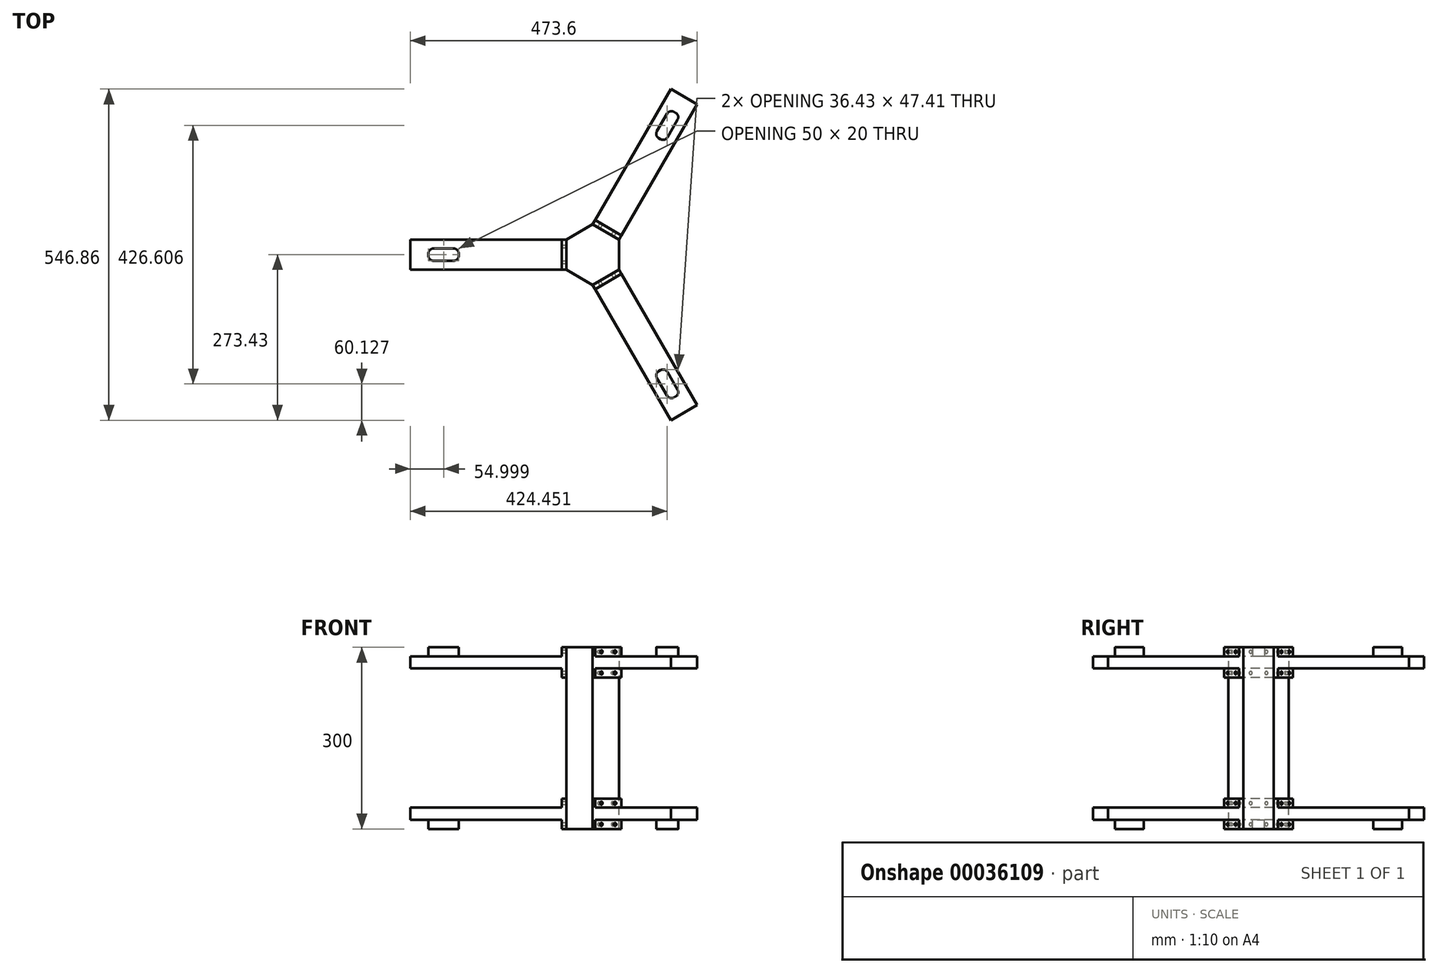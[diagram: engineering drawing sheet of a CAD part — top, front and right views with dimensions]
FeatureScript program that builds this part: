
annotation { "Feature Type Name" : "Feature", "Feature Type Description" : "" }
export const myFeature = defineFeature(function(context is Context, id is Id, definition is map)
    precondition{}
    {
        {
            var Q0;
            Q0=qCreatedBy(makeId("Top.planeOp"),FACE);
            var sketch = newSketch(context, id + "F0", { "sketchPlane" : qUnion([Q0])});
            skCircle(sketch, "E0.cCircle", {"center": v(0, 0) * mm, "radius": 50 * mm, "construction": true});
            skLineSegment(sketch, "E0.0", {"start": v(-43.3, 25) * mm, "end": v(0, 50) * mm});
            skLineSegment(sketch, "E0.1", {"start": v(0, 50) * mm, "end": v(43.3, 25) * mm});
            skLineSegment(sketch, "E0.2", {"start": v(43.3, 25) * mm, "end": v(43.3, -25) * mm});
            skLineSegment(sketch, "E0.3", {"start": v(43.3, -25) * mm, "end": v(0, -50) * mm});
            skLineSegment(sketch, "E0.4", {"start": v(0, -50) * mm, "end": v(-43.3, -25) * mm});
            skLineSegment(sketch, "E0.5", {"start": v(-43.3, -25) * mm, "end": v(-43.3, 25) * mm});
            skLineSegment(sketch, "E1", {"start": v(0, 50) * mm, "end": v(0, 0) * mm, "construction": true});
            skSolve(sketch);
        }
        {
            var Q0;
            Q0 = qSketchRegion(id + "F0", true);
            extrude(context, id + "F1", {"entities" : qUnion([Q0]), "endBound" : BoundingType.SYMMETRIC, "depth" : 300 * mm});
        }
        {
            var Q0;
            Q0=makeQuery(id+"F1.opExtrude","SWEPT_FACE",FACE,{"disambiguationData":[OSD([sQuery(id+"F0.wireOp",EDGE,"E0.3")])]});
            var sketch = newSketch(context, id + "F2", { "sketchPlane" : qUnion([Q0])});
            skLineSegment(sketch, "E2.bottom", {"start": v(-25, 150) * mm, "end": v(25, 150) * mm});
            skLineSegment(sketch, "E2.top", {"start": v(-25, 100) * mm, "end": v(25, 100) * mm});
            skLineSegment(sketch, "E2.left", {"start": v(-25, 150) * mm, "end": v(-25, 100) * mm});
            skLineSegment(sketch, "E2.right", {"start": v(25, 150) * mm, "end": v(25, 100) * mm});
            skSolve(sketch);
        }
        {
            var Q0;
            Q0=makeQuery(id+"F2.imprint","IMPRINT",FACE,{"disambiguationData":[TD([[makeQuery(id+"F2.imprint","IMPRINT",EDGE,{"derivedFrom":sQuery(id+"F2.wireOp",EDGE,"E2.bottom")}),1.0]])]});
            extrude(context, id + "F3", {"entities" : qUnion([Q0]), "depth" : 8 * mm});
        }
        {
            var Q0;
            Q0=makeQuery(id+"F3.opExtrude","CAP_FACE",FACE,{"disambiguationData":[OSD([sQuery(id+"F2.wireOp",EDGE,"E2.bottom"),sQuery(id+"F2.wireOp",EDGE,"E2.top"),sQuery(id+"F2.wireOp",EDGE,"E2.left"),sQuery(id+"F2.wireOp",EDGE,"E2.right")])],"isStart":false});
            var sketch = newSketch(context, id + "F4", { "sketchPlane" : qUnion([Q0])});
            skLineSegment(sketch, "E3.bottom", {"start": v(-25, 135) * mm, "end": v(25, 135) * mm});
            skLineSegment(sketch, "E3.top", {"start": v(-25, 115) * mm, "end": v(25, 115) * mm});
            skLineSegment(sketch, "E3.left", {"start": v(-25, 135) * mm, "end": v(-25, 115) * mm});
            skLineSegment(sketch, "E3.right", {"start": v(25, 135) * mm, "end": v(25, 115) * mm});
            skPoint(sketch, "E4", {"position": v(-25, 125) * mm});
            skSolve(sketch);
        }
        {
            var Q0;
            Q0 = qSketchRegion(id + "F4", true);
            extrude(context, id + "F5", {"entities" : qUnion([Q0]), "operationType" : NewBodyOperationType.ADD, "depth" : 250 * mm});
        }
        {
            var Q0;
            Q0=makeQuery(id+"F5.opExtrude","SWEPT_FACE",FACE,{"disambiguationData":[OSD([sQuery(id+"F4.wireOp",EDGE,"E3.bottom")])]});
            var Q1;
            Q1=makeQuery(id+"F5.opExtrude","SWEPT_FACE",FACE,{"disambiguationData":[OSD([sQuery(id+"F4.wireOp",EDGE,"E3.top")])]});
            cPlane(context, id + "F6", {"entities" : qUnion([Q0, Q1]), "cplaneType" : CPlaneType.MID_PLANE, "offset" : 150 * mm, "width" : 150 * mm, "height" : 150 * mm});
        }
        {
            var Q0;
            {var subQ0=sQuery(id+"F2.wireOp",EDGE,"E2.bottom");var subQ1=sQuery(id+"F2.wireOp",EDGE,"E2.left");var subQ2=sQuery(id+"F2.wireOp",EDGE,"E2.right");Q0=makeQuery(id+"F5.boolean.opBoolean","SPLIT",FACE,{"disambiguationData":[TD([makeQuery(id+"F3.opExtrude","SWEPT_FACE",FACE,{"disambiguationData":[OSD([subQ0])]})])],"derivedFrom":makeQuery(id+"F3.opExtrude","CAP_FACE",FACE,{"disambiguationData":[OSD([subQ0,sQuery(id+"F2.wireOp",EDGE,"E2.top"),subQ1,subQ2])],"isStart":false})});}
            var sketch = newSketch(context, id + "F7", { "sketchPlane" : qUnion([Q0])});
            skPoint(sketch, "E5", {"position": v(-13, 142.5) * mm});
            skPoint(sketch, "E6", {"position": v(13, 142.5) * mm});
            skLineSegment(sketch, "E7", {"start": v(-25, 142.5) * mm, "end": v(-13, 142.5) * mm});
            skLineSegment(sketch, "E8", {"start": v(13, 142.5) * mm, "end": v(-13, 142.5) * mm});
            skLineSegment(sketch, "E9", {"start": v(13, 142.5) * mm, "end": v(25, 142.5) * mm});
            skPoint(sketch, "E10.MirrorP", {"position": v(-13, 107.5) * mm});
            skPoint(sketch, "E11.MirrorP", {"position": v(13, 107.5) * mm});
            skSolve(sketch);
        }
        {
            var Q0;
            Q0=sQuery(id+"F7.wireOp",VERTEX,"E5");
            var Q1;
            Q1=sQuery(id+"F7.wireOp",VERTEX,"E6");
            var Q2;
            Q2=sQuery(id+"F7.wireOp",VERTEX,"E10.MirrorP");
            var Q3;
            Q3=sQuery(id+"F7.wireOp",VERTEX,"E11.MirrorP");
            var Q4;
            Q4=makeQuery(id+"F3.opExtrude","SWEPT_BODY",BODY,{"disambiguationData":[OSD([sQuery(id+"F2.wireOp",EDGE,"E2.bottom"),sQuery(id+"F2.wireOp",EDGE,"E2.top"),sQuery(id+"F2.wireOp",EDGE,"E2.left"),sQuery(id+"F2.wireOp",EDGE,"E2.right")])]});
            hole(context, id + "F8", {"style" : HoleStyle.SIMPLE, "holeDiameter" : 5 * mm, "endStyle" : HoleEndStyle.THROUGH, "locations" : qUnion([Q0, Q1, Q2, Q3]), "scope" : qUnion([Q4])});
        }
        {
            var Q0;
            Q0=makeQuery(id+"F5.opExtrude","SWEPT_FACE",FACE,{"disambiguationData":[OSD([sQuery(id+"F4.wireOp",EDGE,"E3.bottom")])]});
            var sketch = newSketch(context, id + "F9", { "sketchPlane" : qUnion([Q0])});
            skLineSegment(sketch, "E12", {"start": v(133.92, -235.95) * mm, "end": v(137.38, -233.95) * mm});
            skLineSegment(sketch, "E13", {"start": v(140.31, -223.03) * mm, "end": v(123.31, -193.58) * mm});
            skLineSegment(sketch, "E14", {"start": v(112.38, -190.65) * mm, "end": v(108.92, -192.65) * mm});
            skLineSegment(sketch, "E15", {"start": v(106, -203.58) * mm, "end": v(123, -233.03) * mm});
            skPoint(sketch, "E16", {"position": v(150.65, -260.93) * mm});
            skLineSegment(sketch, "E17", {"start": v(150.65, -260.93) * mm, "end": v(135.65, -234.95) * mm, "construction": true});
            skPoint(sketch, "E18.visualSharp", {"position": v(127, -239.95) * mm});
            skArc(sketch, "E18.filletArc", {"start": v(123, -233.03) * mm, "mid": v(127.85, -236.75) * mm, "end": v(133.92, -235.95) * mm});
            skPoint(sketch, "E19.visualSharp", {"position": v(144.31, -229.95) * mm});
            skArc(sketch, "E19.filletArc", {"start": v(137.38, -233.95) * mm, "mid": v(141.11, -229.1) * mm, "end": v(140.31, -223.03) * mm});
            skPoint(sketch, "E20.visualSharp", {"position": v(119.31, -186.65) * mm});
            skArc(sketch, "E20.filletArc", {"start": v(123.31, -193.58) * mm, "mid": v(118.45, -189.85) * mm, "end": v(112.38, -190.65) * mm});
            skPoint(sketch, "E21.visualSharp", {"position": v(102, -196.65) * mm});
            skArc(sketch, "E21.filletArc", {"start": v(108.92, -192.65) * mm, "mid": v(105.2, -197.51) * mm, "end": v(106, -203.58) * mm});
            skSolve(sketch);
        }
        {
            var Q0;
            Q0 = qSketchRegion(id + "F9", true);
            extrude(context, id + "F10", {"entities" : qUnion([Q0]), "operationType" : NewBodyOperationType.ADD, "depth" : 15 * mm});
        }
        {
            var Q0;
            Q0=makeQuery(id+"F3.opExtrude","SWEPT_BODY",BODY,{"disambiguationData":[OSD([sQuery(id+"F2.wireOp",EDGE,"E2.bottom"),sQuery(id+"F2.wireOp",EDGE,"E2.top"),sQuery(id+"F2.wireOp",EDGE,"E2.left"),sQuery(id+"F2.wireOp",EDGE,"E2.right")])]});
            var Q1;
            Q1=sQuery(id+"F0.wireOp",EDGE,"E0.cCircle");
            circularPattern(context, id + "F11", {"entities" : qUnion([Q0]), "axis" : qUnion([Q1]), "angle" : 360 * degree, "instanceCount" : 3, "equalSpace" : true});
        }
        {
            var Q0;
            Q0=makeQuery(id+"F11.opPattern","COPY",BODY,{"derivedFrom":makeQuery(id+"F3.opExtrude","SWEPT_BODY",BODY,{"disambiguationData":[OSD([sQuery(id+"F2.wireOp",EDGE,"E2.bottom"),sQuery(id+"F2.wireOp",EDGE,"E2.top"),sQuery(id+"F2.wireOp",EDGE,"E2.left"),sQuery(id+"F2.wireOp",EDGE,"E2.right")])]}),"instanceName":"2"});
            var Q1;
            Q1=makeQuery(id+"F11.opPattern","COPY",BODY,{"derivedFrom":makeQuery(id+"F3.opExtrude","SWEPT_BODY",BODY,{"disambiguationData":[OSD([sQuery(id+"F2.wireOp",EDGE,"E2.bottom"),sQuery(id+"F2.wireOp",EDGE,"E2.top"),sQuery(id+"F2.wireOp",EDGE,"E2.left"),sQuery(id+"F2.wireOp",EDGE,"E2.right")])]}),"instanceName":"1"});
            var Q2;
            Q2=makeQuery(id+"F3.opExtrude","SWEPT_BODY",BODY,{"disambiguationData":[OSD([sQuery(id+"F2.wireOp",EDGE,"E2.bottom"),sQuery(id+"F2.wireOp",EDGE,"E2.top"),sQuery(id+"F2.wireOp",EDGE,"E2.left"),sQuery(id+"F2.wireOp",EDGE,"E2.right")])]});
            var Q3;
            Q3=qCreatedBy(makeId("Top.planeOp"),FACE);
            mirror(context, id + "F12", {"entities" : qUnion([Q0, Q1, Q2]), "mirrorPlane" : qUnion([Q3])});
        }
    });
